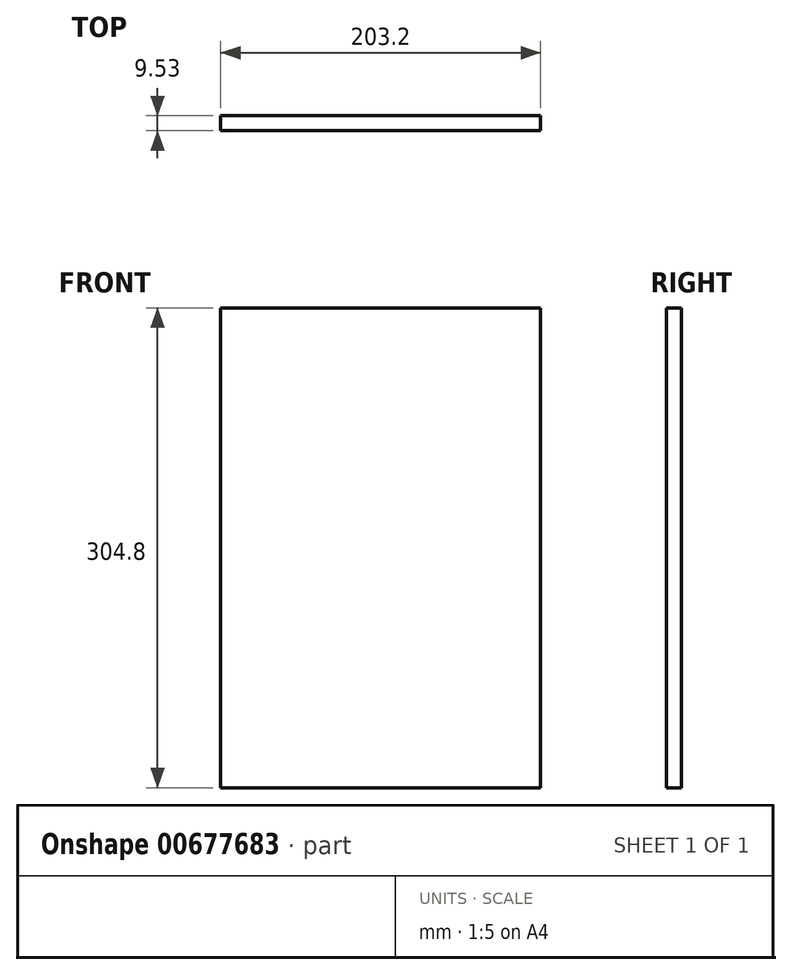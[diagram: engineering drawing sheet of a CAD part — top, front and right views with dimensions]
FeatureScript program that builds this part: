
annotation { "Feature Type Name" : "Feature", "Feature Type Description" : "" }
export const myFeature = defineFeature(function(context is Context, id is Id, definition is map)
    precondition{}
    {
        {
            var Q0;
            Q0=qCreatedBy(makeId("Front.planeOp"),FACE);
            var sketch = newSketch(context, id + "F0", { "sketchPlane" : qUnion([Q0])});
            skLineSegment(sketch, "E0.bottom", {"start": v(0, 0) * mm, "end": v(-203.2, 0) * mm});
            skLineSegment(sketch, "E0.top", {"start": v(0, 304.8) * mm, "end": v(-203.2, 304.8) * mm});
            skLineSegment(sketch, "E0.left", {"start": v(0, 0) * mm, "end": v(0, 304.8) * mm});
            skLineSegment(sketch, "E0.right", {"start": v(-203.2, 0) * mm, "end": v(-203.2, 304.8) * mm});
            skSolve(sketch);
        }
        {
            var Q0;
            Q0=makeQuery(id+"F0.imprint","IMPRINT",FACE,{"disambiguationData":[TD([[makeQuery(id+"F0.imprint","IMPRINT",EDGE,{"derivedFrom":sQuery(id+"F0.wireOp",EDGE,"E0.bottom")}),-1.0]])]});
            extrude(context, id + "F1", {"entities" : qUnion([Q0]), "depth" : 9.52 * mm, "offsetDistance" : 25.4 * mm});
        }
    });
